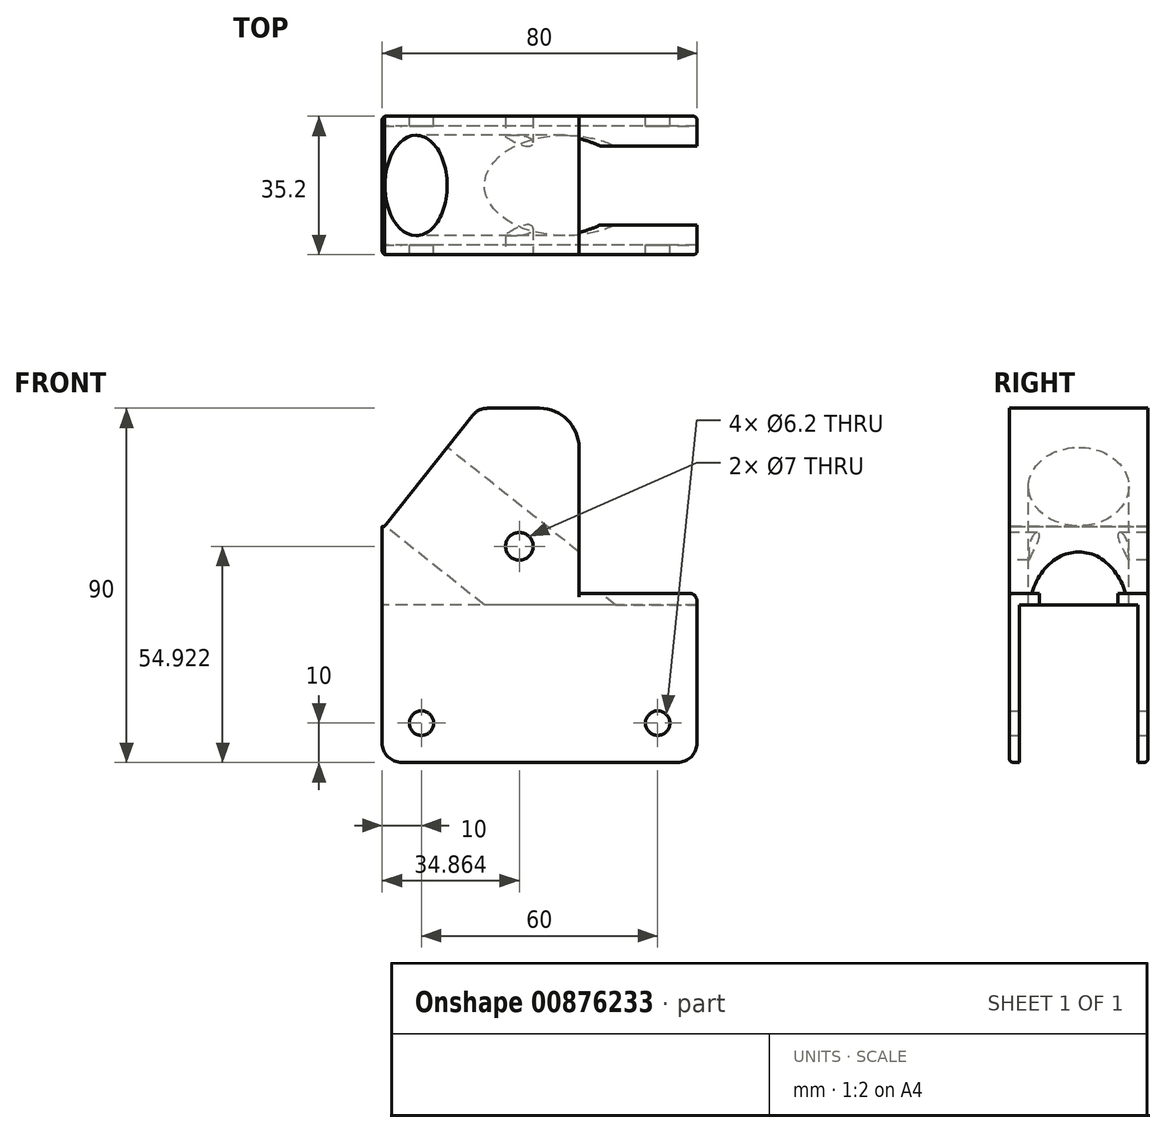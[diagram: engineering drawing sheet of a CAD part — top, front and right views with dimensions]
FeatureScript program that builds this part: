
annotation { "Feature Type Name" : "Feature", "Feature Type Description" : "" }
export const myFeature = defineFeature(function(context is Context, id is Id, definition is map)
    precondition{}
    {
        {
            var Q0;
            Q0=qCreatedBy(makeId("Front.planeOp"),FACE);
            var sketch = newSketch(context, id + "F0", { "sketchPlane" : qUnion([Q0])});
            skLineSegment(sketch, "E0.bottom", {"start": v(40, -21.5) * mm, "end": v(-40, -21.5) * mm});
            skLineSegment(sketch, "E0.top", {"start": v(40, 21.5) * mm, "end": v(10, 21.5) * mm});
            skLineSegment(sketch, "E0.left", {"start": v(40, -21.5) * mm, "end": v(40, 21.5) * mm});
            skLineSegment(sketch, "E0.right", {"start": v(-40, -21.5) * mm, "end": v(-40, 21.5) * mm});
            skPoint(sketch, "E0.middle", {"position": v(0, 0) * mm});
            skLineSegment(sketch, "E1.top", {"start": v(-13.18, 68.5) * mm, "end": v(10, 68.5) * mm});
            skLineSegment(sketch, "E1.left", {"start": v(-40, 21.5) * mm, "end": v(-40, 38.5) * mm});
            skLineSegment(sketch, "E1.right", {"start": v(10, 21.5) * mm, "end": v(10, 68.5) * mm});
            skPoint(sketch, "E2.orphan", {"position": v(-26.69, 60.53) * mm});
            skLineSegment(sketch, "E3", {"start": v(-40, 38.5) * mm, "end": v(-39.33, 38.5) * mm});
            skLineSegment(sketch, "E4", {"start": v(-39.39, 38.53) * mm, "end": v(-17.1, 66.6) * mm});
            skArc(sketch, "E5.filletArc", {"start": v(-13.18, 68.5) * mm, "mid": v(-15.35, 68) * mm, "end": v(-17.1, 66.6) * mm});
            skLineSegment(sketch, "E6.trimOffspring", {"start": v(-40, 68.22) * mm, "end": v(-40.5, 68.5) * mm});
            skLineSegment(sketch, "E7.trimOffspring", {"start": v(-40, 68.22) * mm, "end": v(-40, 68.5) * mm});
            skPoint(sketch, "E8.start.orphan", {"position": v(37.6, -66.3) * mm});
            skPoint(sketch, "E9.orphan", {"position": v(77.08, 0.62) * mm});
            skLineSegment(sketch, "E10.trimOffspring", {"start": v(-39.33, 38.5) * mm, "end": v(-39.39, 38.53) * mm});
            skPoint(sketch, "E11.MirrorCS.start.orphan", {"position": v(64.38, -21.38) * mm});
            skPoint(sketch, "E12.orphan", {"position": v(70.73, -10.38) * mm});
            skLineSegment(sketch, "E13", {"start": v(40, 7.36) * mm, "end": v(-33.22, 7.36) * mm, "construction": true});
            skLineSegment(sketch, "E14", {"start": v(-31.4, 48.59) * mm, "end": v(68.82, 48.59) * mm, "construction": true});
            skCircle(sketch, "E15", {"center": v(-30, -11.5) * mm, "radius": 3.1 * mm});
            skCircle(sketch, "E16", {"center": v(30, -11.5) * mm, "radius": 3.1 * mm});
            skSolve(sketch);
        }
        {
            var Q0;
            Q0 = qSketchRegion(id + "F0", true);
            extrude(context, id + "F1", {"entities" : qUnion([Q0]), "endBound" : BoundingType.SYMMETRIC, "depth" : 35.2 * mm, "offsetDistance" : 25 * mm});
        }
        {
            var Q0;
            Q0=qCreatedBy(makeId("Front.planeOp"),FACE);
            var sketch = newSketch(context, id + "F2", { "sketchPlane" : qUnion([Q0])});
            skLineSegment(sketch, "E17.0", {"start": v(40, -21.5) * mm, "end": v(-40, -21.5) * mm});
            skLineSegment(sketch, "E18", {"start": v(40, -21.5) * mm, "end": v(40, 18.5) * mm});
            skLineSegment(sketch, "E19", {"start": v(40, 18.5) * mm, "end": v(-40, 18.5) * mm});
            skLineSegment(sketch, "E20", {"start": v(-40, 18.5) * mm, "end": v(-40, -21.5) * mm});
            skSolve(sketch);
        }
        {
            var Q0;
            Q0 = qSketchRegion(id + "F2", true);
            extrude(context, id + "F3", {"entities" : qUnion([Q0]), "operationType" : NewBodyOperationType.REMOVE, "endBound" : BoundingType.SYMMETRIC, "depth" : 30.2 * mm, "offsetDistance" : 25 * mm});
        }
        {
            var Q0;
            {var subQ0=sQuery(id+"F0.wireOp",EDGE,"E0.bottom");var subQ1=sQuery(id+"F0.wireOp",EDGE,"E0.left");Q0=makeQuery(id+"F3.boolean.opBoolean","SPLIT",EDGE,{"disambiguationData":[TD([makeQuery(id+"F3.opExtrude","CAP_FACE",FACE,{"disambiguationData":[OSD([sQuery(id+"F2.wireOp",EDGE,"E17.0"),sQuery(id+"F2.wireOp",EDGE,"E18"),sQuery(id+"F2.wireOp",EDGE,"E19"),sQuery(id+"F2.wireOp",EDGE,"E20")])],"isStart":true})])],"derivedFrom":makeQuery(id+"F1.opExtrude","SWEPT_EDGE",EDGE,{"disambiguationData":[OSD([subQ0,subQ1])]})});}
            var Q1;
            {var subQ0=sQuery(id+"F0.wireOp",EDGE,"E0.bottom");var subQ1=sQuery(id+"F0.wireOp",EDGE,"E0.left");Q1=makeQuery(id+"F3.boolean.opBoolean","SPLIT",EDGE,{"disambiguationData":[TD([makeQuery(id+"F3.opExtrude","CAP_FACE",FACE,{"disambiguationData":[OSD([sQuery(id+"F2.wireOp",EDGE,"E17.0"),sQuery(id+"F2.wireOp",EDGE,"E18"),sQuery(id+"F2.wireOp",EDGE,"E19"),sQuery(id+"F2.wireOp",EDGE,"E20")])],"isStart":false})])],"derivedFrom":makeQuery(id+"F1.opExtrude","SWEPT_EDGE",EDGE,{"disambiguationData":[OSD([subQ0,subQ1])]})});}
            fillet(context, id + "F4", {"entities" : qUnion([Q0, Q1]), "radius" : 5 * mm, "tangentPropagation" : true, "allowEdgeOverflow" : false});
        }
        {
            var Q0;
            {var subQ0=sQuery(id+"F0.wireOp",EDGE,"E0.bottom");var subQ2=sQuery(id+"F0.wireOp",EDGE,"E0.right");Q0=makeQuery(id+"F3.boolean.opBoolean","SPLIT",EDGE,{"disambiguationData":[TD([makeQuery(id+"F3.opExtrude","CAP_FACE",FACE,{"disambiguationData":[OSD([sQuery(id+"F2.wireOp",EDGE,"E17.0"),sQuery(id+"F2.wireOp",EDGE,"E18"),sQuery(id+"F2.wireOp",EDGE,"E19"),sQuery(id+"F2.wireOp",EDGE,"E20")])],"isStart":false})])],"derivedFrom":makeQuery(id+"F1.opExtrude","SWEPT_EDGE",EDGE,{"disambiguationData":[OSD([subQ0,subQ2])]})});}
            var Q1;
            {var subQ0=sQuery(id+"F0.wireOp",EDGE,"E0.bottom");var subQ2=sQuery(id+"F0.wireOp",EDGE,"E0.right");Q1=makeQuery(id+"F3.boolean.opBoolean","SPLIT",EDGE,{"disambiguationData":[TD([makeQuery(id+"F3.opExtrude","CAP_FACE",FACE,{"disambiguationData":[OSD([sQuery(id+"F2.wireOp",EDGE,"E17.0"),sQuery(id+"F2.wireOp",EDGE,"E18"),sQuery(id+"F2.wireOp",EDGE,"E19"),sQuery(id+"F2.wireOp",EDGE,"E20")])],"isStart":true})])],"derivedFrom":makeQuery(id+"F1.opExtrude","SWEPT_EDGE",EDGE,{"disambiguationData":[OSD([subQ0,subQ2])]})});}
            fillet(context, id + "F5", {"entities" : qUnion([Q0, Q1]), "radius" : 5 * mm, "tangentPropagation" : true, "allowEdgeOverflow" : false});
        }
        {
            var Q0;
            Q0=makeQuery(id+"F1.opExtrude","SWEPT_EDGE",EDGE,{"disambiguationData":[OSD([sQuery(id+"F0.wireOp",EDGE,"E1.top"),sQuery(id+"F0.wireOp",EDGE,"E1.right")])]});
            fillet(context, id + "F6", {"entities" : qUnion([Q0]), "radius" : 10 * mm, "tangentPropagation" : true, "allowEdgeOverflow" : false});
        }
        {
            var Q0;
            Q0=makeQuery(id+"F1.opExtrude","SWEPT_FACE",FACE,{"disambiguationData":[OSD([sQuery(id+"F0.wireOp",EDGE,"E0.top")])]});
            var sketch = newSketch(context, id + "F7", { "sketchPlane" : qUnion([Q0])});
            skLineSegment(sketch, "E21.0", {"start": v(40, -10) * mm, "end": v(40, 10) * mm});
            skLineSegment(sketch, "E22.0", {"start": v(10, -5) * mm, "end": v(10, 5) * mm});
            skLineSegment(sketch, "E23", {"start": v(40, 0) * mm, "end": v(40, 10) * mm});
            skLineSegment(sketch, "E24", {"start": v(40, 10) * mm, "end": v(15, 10) * mm});
            skLineSegment(sketch, "E25.MirrorCS", {"start": v(40, -10) * mm, "end": v(15, -10) * mm});
            skPoint(sketch, "E26.orphan", {"position": v(10, 17.6) * mm});
            skPoint(sketch, "E27.orphan", {"position": v(10, -17.6) * mm});
            skPoint(sketch, "E28.orphan", {"position": v(40, -17.6) * mm});
            skPoint(sketch, "E29.orphan", {"position": v(40, 17.6) * mm});
            skPoint(sketch, "E30.start.orphan", {"position": v(10, 0) * mm});
            skPoint(sketch, "E31.visualSharp", {"position": v(10, 10) * mm});
            skArc(sketch, "E31.filletArc", {"start": v(15, 10) * mm, "mid": v(11.46, 8.54) * mm, "end": v(10, 5) * mm});
            skPoint(sketch, "E32.visualSharp", {"position": v(10, -10) * mm});
            skArc(sketch, "E32.filletArc", {"start": v(10, -5) * mm, "mid": v(11.46, -8.54) * mm, "end": v(15, -10) * mm});
            skSolve(sketch);
        }
        {
            var Q0;
            Q0 = qSketchRegion(id + "F7", true);
            extrude(context, id + "F8", {"entities" : qUnion([Q0]), "operationType" : NewBodyOperationType.REMOVE, "oppositeDirection" : true, "depth" : 5 * mm, "offsetDistance" : 25 * mm});
        }
        {
            var Q0;
            Q0=makeQuery(id+"F1.opExtrude","SWEPT_FACE",FACE,{"disambiguationData":[OSD([sQuery(id+"F0.wireOp",EDGE,"E4")])]});
            var sketch = newSketch(context, id + "F9", { "sketchPlane" : qUnion([Q0])});
            skPoint(sketch, "E33.0", {"position": v(0, 18.53) * mm});
            skCircle(sketch, "E34", {"center": v(0, 18.53) * mm, "radius": 12.75 * mm});
            skSolve(sketch);
        }
        {
            var Q0;
            Q0 = qSketchRegion(id + "F9", true);
            extrude(context, id + "F10", {"entities" : qUnion([Q0]), "operationType" : NewBodyOperationType.REMOVE, "endBound" : BoundingType.THROUGH_ALL, "oppositeDirection" : true, "depth" : 49.5 * mm, "offsetDistance" : 25 * mm});
        }
        {
            var Q0;
            {var subQ0=sQuery(id+"F0.wireOp",EDGE,"E0.left");var subQ1=sQuery(id+"F0.wireOp",EDGE,"E0.top");Q0=makeQuery(id+"F8.boolean.opBoolean","SPLIT",EDGE,{"disambiguationData":[TD([makeQuery(id+"F8.opExtrude","SWEPT_FACE",FACE,{"disambiguationData":[OSD([sQuery(id+"F7.wireOp",EDGE,"E24")])]})])],"derivedFrom":makeQuery(id+"F1.opExtrude","SWEPT_EDGE",EDGE,{"disambiguationData":[OSD([subQ1,subQ0])]})});}
            var Q1;
            {var subQ0=sQuery(id+"F0.wireOp",EDGE,"E0.left");var subQ1=sQuery(id+"F0.wireOp",EDGE,"E0.top");Q1=makeQuery(id+"F8.boolean.opBoolean","SPLIT",EDGE,{"disambiguationData":[TD([makeQuery(id+"F8.opExtrude","SWEPT_FACE",FACE,{"disambiguationData":[OSD([sQuery(id+"F7.wireOp",EDGE,"E25.MirrorCS")])]})])],"derivedFrom":makeQuery(id+"F1.opExtrude","SWEPT_EDGE",EDGE,{"disambiguationData":[OSD([subQ1,subQ0])]})});}
            fillet(context, id + "F11", {"entities" : qUnion([Q0, Q1]), "radius" : 2 * mm, "tangentPropagation" : true, "allowEdgeOverflow" : false});
        }
        {
            var Q0;
            Q0=makeQuery(id+"F1.opExtrude","CAP_EDGE",EDGE,{"disambiguationData":[OSD([sQuery(id+"F0.wireOp",EDGE,"E0.left")])],"isStart":false});
            var Q1;
            Q1=makeQuery(id+"F1.opExtrude","CAP_EDGE",EDGE,{"disambiguationData":[OSD([sQuery(id+"F0.wireOp",EDGE,"E0.left")])],"isStart":true});
            fillet(context, id + "F12", {"entities" : qUnion([Q0, Q1]), "radius" : 1 * mm, "tangentPropagation" : true, "allowEdgeOverflow" : false});
        }
        {
            var Q0;
            Q0=makeQuery(id+"F1.opExtrude","CAP_FACE",FACE,{"disambiguationData":[OSD([sQuery(id+"F0.wireOp",EDGE,"E0.bottom"),sQuery(id+"F0.wireOp",EDGE,"E0.top"),sQuery(id+"F0.wireOp",EDGE,"E0.left"),sQuery(id+"F0.wireOp",EDGE,"E0.right"),sQuery(id+"F0.wireOp",EDGE,"E1.top"),sQuery(id+"F0.wireOp",EDGE,"E1.left"),sQuery(id+"F0.wireOp",EDGE,"E1.right"),sQuery(id+"F0.wireOp",EDGE,"E3"),sQuery(id+"F0.wireOp",EDGE,"E4"),sQuery(id+"F0.wireOp",EDGE,"E5.filletArc"),sQuery(id+"F0.wireOp",EDGE,"E10.trimOffspring"),sQuery(id+"F0.wireOp",EDGE,"E15"),sQuery(id+"F0.wireOp",EDGE,"E16")])],"isStart":false});
            var sketch = newSketch(context, id + "F13", { "sketchPlane" : qUnion([Q0])});
            skPoint(sketch, "E35.0", {"position": v(-28.05, 52.81) * mm});
            skCircle(sketch, "E36", {"center": v(-5.14, 33.42) * mm, "radius": 3.5 * mm});
            skSolve(sketch);
        }
        {
            var Q0;
            Q0 = qSketchRegion(id + "F13", true);
            extrude(context, id + "F14", {"entities" : qUnion([Q0]), "operationType" : NewBodyOperationType.REMOVE, "oppositeDirection" : true, "depth" : 40 * mm, "offsetDistance" : 25 * mm});
        }
    });
